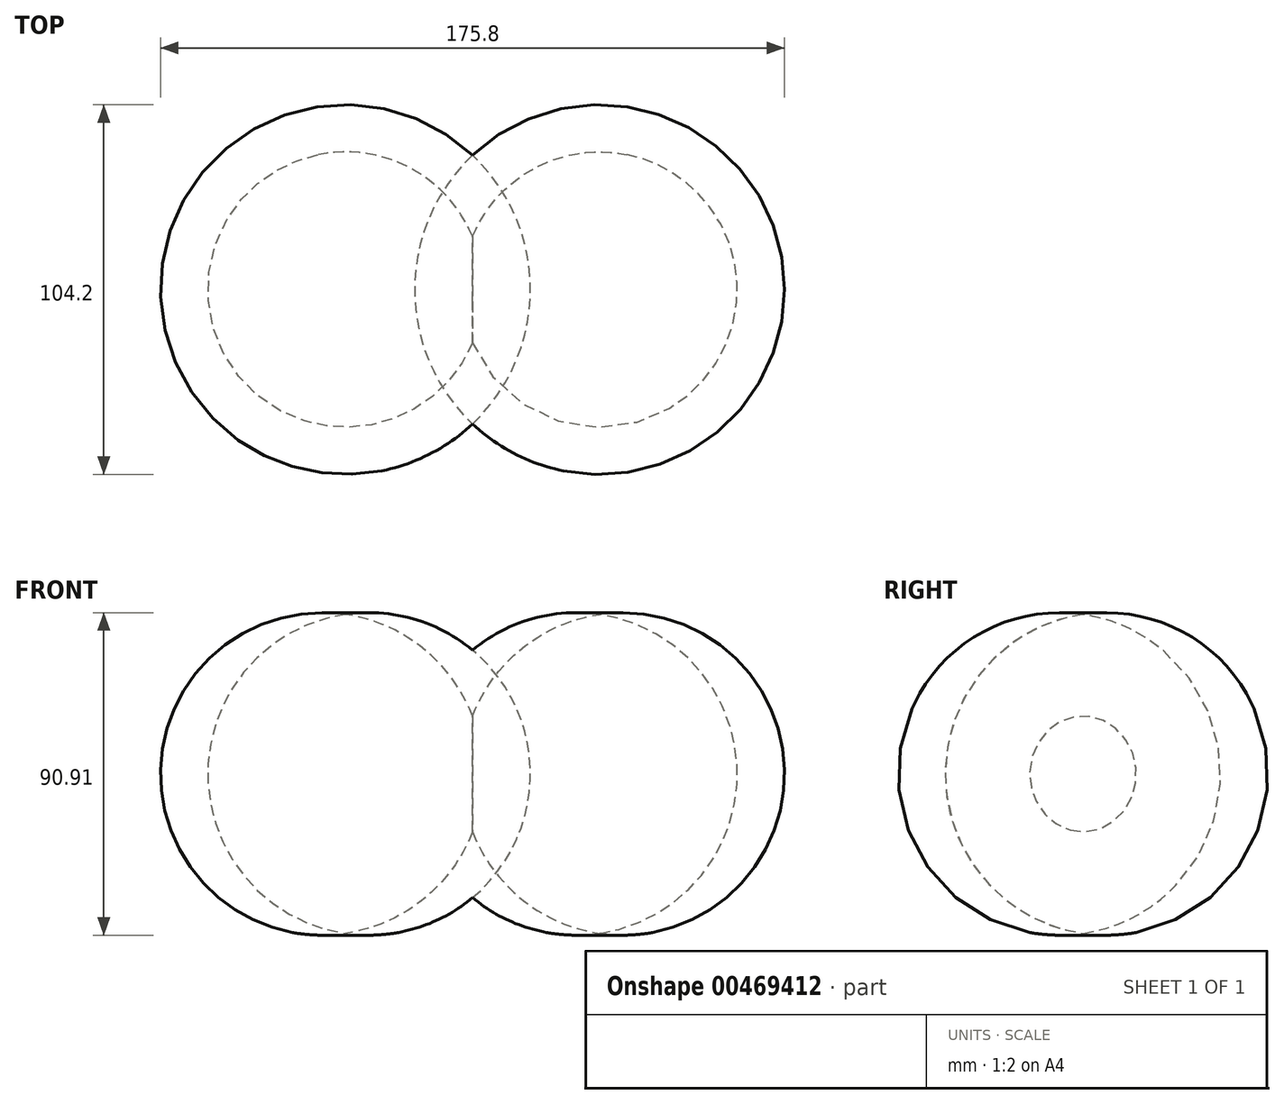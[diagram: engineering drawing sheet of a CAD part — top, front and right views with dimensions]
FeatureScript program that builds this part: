
annotation { "Feature Type Name" : "Feature", "Feature Type Description" : "" }
export const myFeature = defineFeature(function(context is Context, id is Id, definition is map)
    precondition{}
    {
        {
            var Q0;
            Q0=qCreatedBy(makeId("Front.planeOp"),FACE);
            var sketch = newSketch(context, id + "F0", { "sketchPlane" : qUnion([Q0])});
            skLineSegment(sketch, "E0", {"start": v(-35.8, 55.65) * mm, "end": v(-35.8, -34.3) * mm});
            skArc(sketch, "E1", {"start": v(-35.8, -34.3) * mm, "mid": v(3.02, 10.68) * mm, "end": v(-35.8, 55.65) * mm});
            skSolve(sketch);
        }
        {
            var Q0;
            Q0=makeQuery(id+"F0.imprint","IMPRINT",FACE,{"disambiguationData":[TD([[makeQuery(id+"F0.imprint","IMPRINT",EDGE,{"derivedFrom":sQuery(id+"F0.wireOp",EDGE,"E0")}),1.0]])]});
            var Q1;
            Q1=sQuery(id+"F0.wireOp",EDGE,"E0");
            revolve(context, id + "F1", {"entities" : qUnion([Q0]), "axis" : qUnion([Q1]), "revolveType" : RevolveType.FULL});
        }
        {
            var Q0;
            Q0=makeQuery(id+"F1.opRevolve","SWEPT_BODY",BODY,{"disambiguationData":[OSD([sQuery(id+"F0.wireOp",EDGE,"E0"),sQuery(id+"F0.wireOp",EDGE,"E1")])]});
            var Q1;
            Q1=qCreatedBy(makeId("Right.planeOp"),FACE);
            mirror(context, id + "F2", {"operationType" : NewBodyOperationType.ADD, "entities" : qUnion([Q0]), "mirrorPlane" : qUnion([Q1])});
        }
    });
